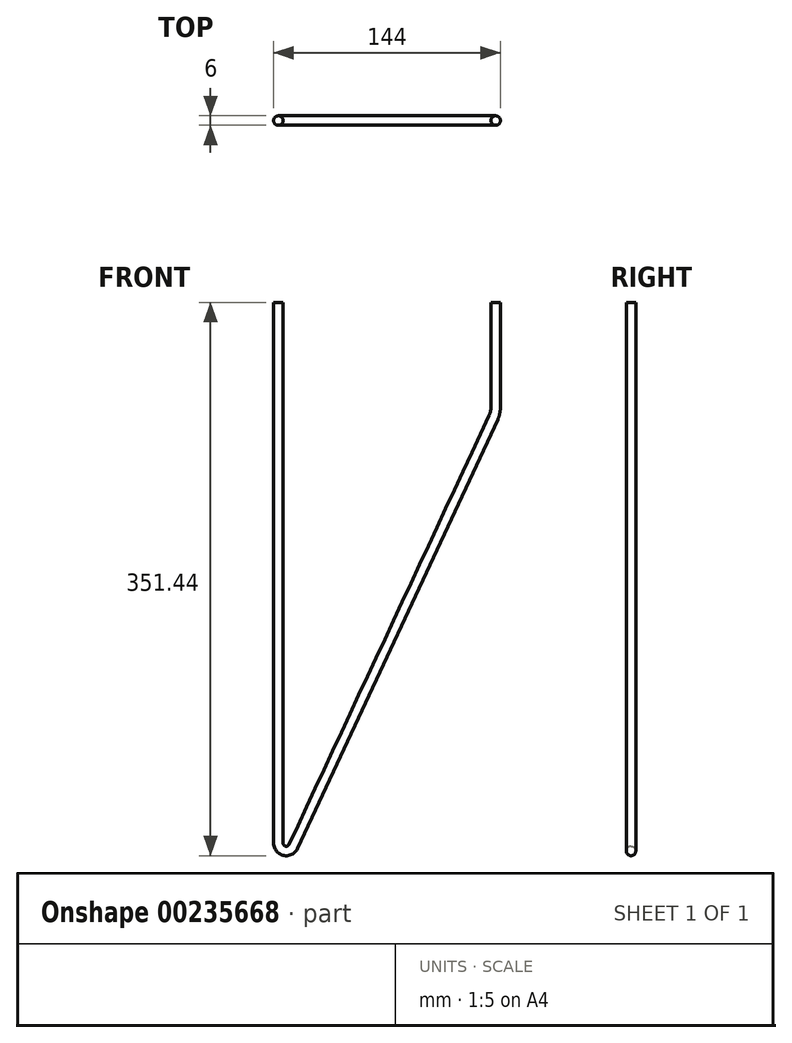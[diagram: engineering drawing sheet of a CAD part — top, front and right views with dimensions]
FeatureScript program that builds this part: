
annotation { "Feature Type Name" : "Feature", "Feature Type Description" : "" }
export const myFeature = defineFeature(function(context is Context, id is Id, definition is map)
    precondition{}
    {
        {
            var Q0;
            Q0=qCreatedBy(makeId("Front.planeOp"),FACE);
            var sketch = newSketch(context, id + "F0", { "sketchPlane" : qUnion([Q0])});
            skLineSegment(sketch, "E0", {"start": v(-65.22, 0) * mm, "end": v(-65.22, -343.44) * mm});
            skLineSegment(sketch, "E1", {"start": v(72.78, -66.68) * mm, "end": v(72.78, 0) * mm});
            skLineSegment(sketch, "E2", {"start": v(71.38, -73.01) * mm, "end": v(-55.69, -345.56) * mm});
            skPoint(sketch, "E3.visualSharp", {"position": v(-65.22, -366) * mm});
            skArc(sketch, "E3.filletArc", {"start": v(-65.22, -343.44) * mm, "mid": v(-61.3, -348.32) * mm, "end": v(-55.69, -345.56) * mm});
            skPoint(sketch, "E4.visualSharp", {"position": v(72.78, -70) * mm});
            skArc(sketch, "E4.filletArc", {"start": v(71.38, -73.01) * mm, "mid": v(72.43, -69.92) * mm, "end": v(72.78, -66.68) * mm});
            skSolve(sketch);
        }
        {
            var Q0;
            Q0=qCreatedBy(makeId("Top.planeOp"),FACE);
            var sketch = newSketch(context, id + "F1", { "sketchPlane" : qUnion([Q0])});
            skCircle(sketch, "E5", {"center": v(-65.22, 0) * mm, "radius": 3 * mm});
            skSolve(sketch);
        }
        {
            var Q0;
            Q0 = qSketchRegion(id + "F1", true);
            var Q1;
            Q1 = qConstructionFilter(qBodyType(qCreatedBy(id + "F0" ,EDGE), BodyType.WIRE), ConstructionObject.NO);
            sweep(context, id + "F2", {"profiles" : qUnion([Q0]), "path" : qUnion([Q1])});
        }
    });
